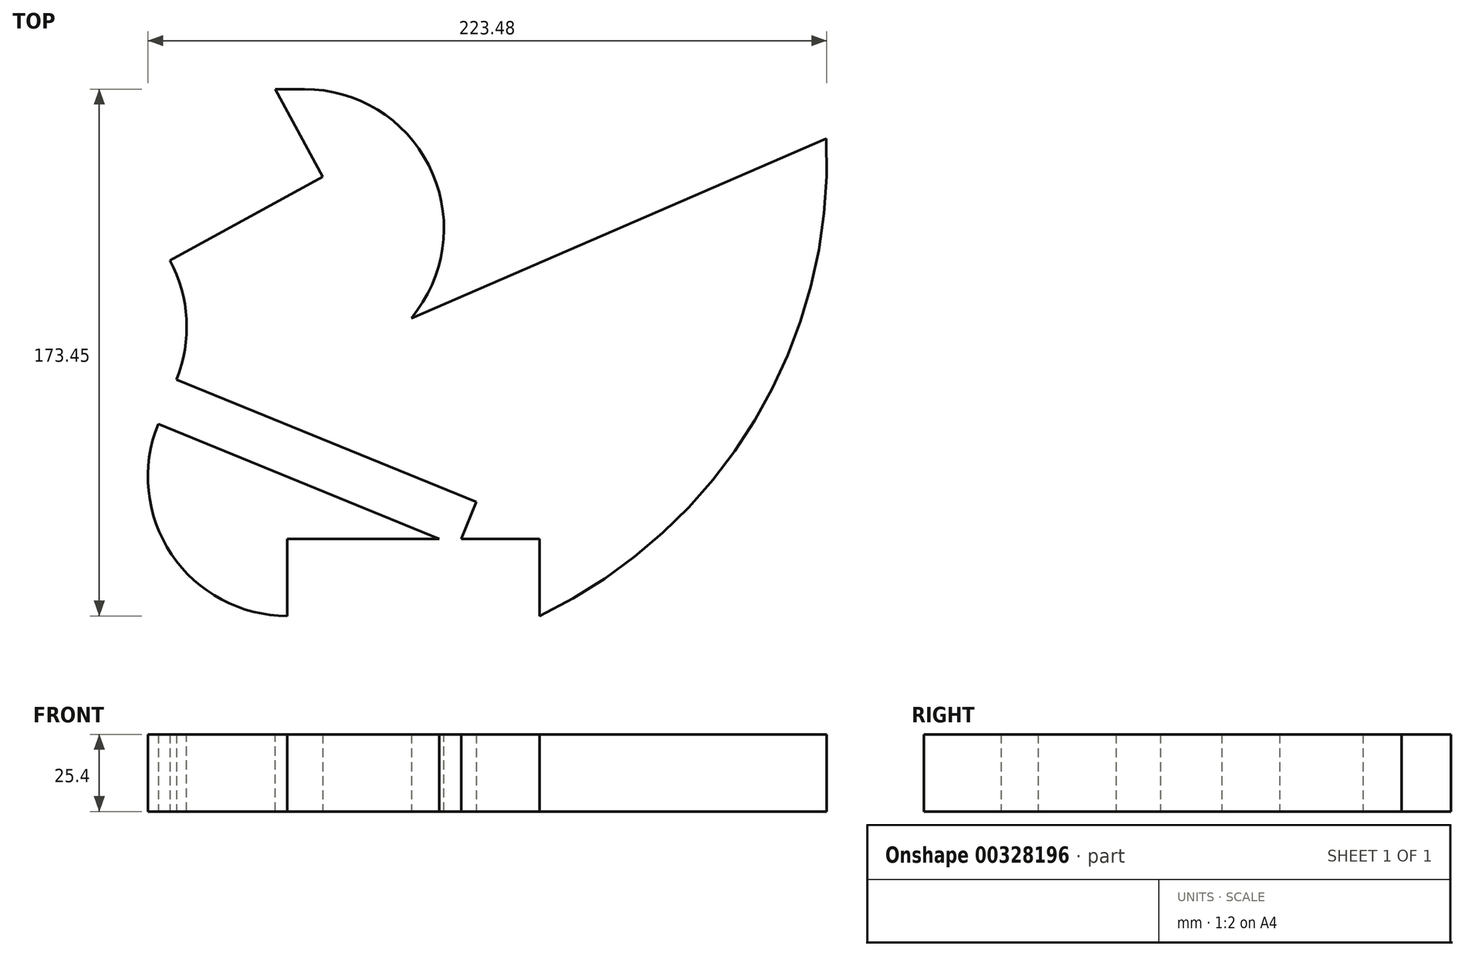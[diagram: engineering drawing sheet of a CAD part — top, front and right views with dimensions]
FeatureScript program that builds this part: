
annotation { "Feature Type Name" : "Feature", "Feature Type Description" : "" }
export const myFeature = defineFeature(function(context is Context, id is Id, definition is map)
    precondition{}
    {
        {
            var Q0;
            Q0=qCreatedBy(makeId("Top.planeOp"),FACE);
            var sketch = newSketch(context, id + "F0", { "sketchPlane" : qUnion([Q0])});
            skFitSpline(sketch, "E0", {"points": [v(0, 0) * mm, v(-35.04, 21.7) * mm, v(0, 48.8) * mm, v(34.1, 21.7) * mm, v(0, 0) * mm]});
            skLineSegment(sketch, "E1", {"start": v(0, 48.8) * mm, "end": v(0, 97.18) * mm});
            skLineSegment(sketch, "E2", {"start": v(0, 97.18) * mm, "end": v(88.91, 97.18) * mm});
            skLineSegment(sketch, "E3", {"start": v(88.91, 97.18) * mm, "end": v(34.1, 21.7) * mm});
            skLineSegment(sketch, "E4", {"start": v(0, 97.18) * mm, "end": v(-76.13, 97.18) * mm});
            skLineSegment(sketch, "E5", {"start": v(-76.13, 97.18) * mm, "end": v(-35.04, 21.7) * mm});
            skLineSegment(sketch, "E6", {"start": v(0, 0) * mm, "end": v(-75.04, -76.27) * mm});
            skLineSegment(sketch, "E7", {"start": v(-75.04, -76.27) * mm, "end": v(76.57, -76.27) * mm});
            skLineSegment(sketch, "E8", {"start": v(76.57, -76.27) * mm, "end": v(0, 0) * mm});
            skLineSegment(sketch, "E9", {"start": v(-35.04, 21.7) * mm, "end": v(-75.04, -76.27) * mm});
            skLineSegment(sketch, "E10", {"start": v(34.1, 21.7) * mm, "end": v(76.57, -76.27) * mm});
            skSolve(sketch);
        }
        {
            var Q0;
            Q0 = qSketchRegion(id + "F0", true);
            extrude(context, id + "F1", {"entities" : qUnion([Q0]), "depth" : 25.4 * mm});
        }
        {
            var Q0;
            Q0=makeQuery(id+"F1.opExtrude","SWEPT_EDGE",EDGE,{"disambiguationData":[OSD([sQuery(id+"F0.wireOp",EDGE,"E2"),sQuery(id+"F0.wireOp",EDGE,"E3")])]});
            var Q1;
            Q1=makeQuery(id+"F1.opExtrude","SWEPT_EDGE",EDGE,{"disambiguationData":[OSD([sQuery(id+"F0.wireOp",EDGE,"E0"),sQuery(id+"F0.wireOp",EDGE,"E5"),sQuery(id+"F0.wireOp",EDGE,"E9")])]});
            var Q2;
            Q2=makeQuery(id+"F1.opExtrude","SWEPT_EDGE",EDGE,{"disambiguationData":[OSD([sQuery(id+"F0.wireOp",EDGE,"E6"),sQuery(id+"F0.wireOp",EDGE,"E7"),sQuery(id+"F0.wireOp",EDGE,"E9")])]});
            fillet(context, id + "F2", {"entities" : qUnion([Q0, Q1, Q2]), "radius" : 45.85 * mm, "tangentPropagation" : true, "allowEdgeOverflow" : false});
        }
        {
            var Q0;
            Q0=makeQuery(id+"F1.opExtrude","SWEPT_FACE",FACE,{"disambiguationData":[OSD([sQuery(id+"F0.wireOp",EDGE,"E10")])]});
            extrude(context, id + "F3", {"entities" : qUnion([Q0]), "operationType" : NewBodyOperationType.ADD, "depth" : 148.84 * mm});
        }
        {
            var Q0;
            Q0=makeQuery(id+"F1.opExtrude","SWEPT_FACE",FACE,{"disambiguationData":[OSD([sQuery(id+"F0.wireOp",EDGE,"E9")])]});
            extrude(context, id + "F4", {"entities" : qUnion([Q0]), "operationType" : NewBodyOperationType.REMOVE, "oppositeDirection" : true, "depth" : 106.68 * mm});
        }
        {
            var Q0;
            Q0=makeQuery(id+"F1.opExtrude","SWEPT_FACE",FACE,{"disambiguationData":[OSD([sQuery(id+"F0.wireOp",EDGE,"E5")])]});
            extrude(context, id + "F5", {"entities" : qUnion([Q0]), "operationType" : NewBodyOperationType.REMOVE, "oppositeDirection" : true, "depth" : 57.4 * mm});
        }
        {
            var Q0;
            Q0=makeQuery(id+"F3.opExtrude","CAP_EDGE",EDGE,{"disambiguationData":[OSD([sQuery(id+"F0.wireOp",EDGE,"E7"),sQuery(id+"F0.wireOp",EDGE,"E8"),sQuery(id+"F0.wireOp",EDGE,"E10")])],"isStart":false});
            fillet(context, id + "F6", {"entities" : qUnion([Q0]), "radius" : 166.18 * mm, "tangentPropagation" : true, "allowEdgeOverflow" : false});
        }
        {
            var Q0;
            Q0=makeQuery(id+"F1.opExtrude","SWEPT_FACE",FACE,{"disambiguationData":[OSD([sQuery(id+"F0.wireOp",EDGE,"E7")])]});
            extrude(context, id + "F7", {"entities" : qUnion([Q0]), "operationType" : NewBodyOperationType.REMOVE, "oppositeDirection" : true, "depth" : 25.4 * mm});
        }
    });
